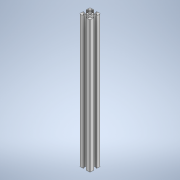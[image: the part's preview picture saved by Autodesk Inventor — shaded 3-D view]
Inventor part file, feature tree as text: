
AUTODESK INVENTOR PART (.ipt)
format: ipt  version: 2020 (Build 240168000, 168)  size: 164,352 bytes
history: native  units: mm
features: extrude x1, fillet x1, sketch x1
ambient origin geometry x8: Origin, YZ Plane, XZ Plane, XY Plane, X Axis, Y Axis, Z Axis, Center Point
bodies: Solide1 (feature_tree)
feature tree (3):
  extrude  "Extrusion1"  Depth=5.0mm
  fillet  "Congé1"  Radius=3.0mm
  sketch  "Esquisse1"
